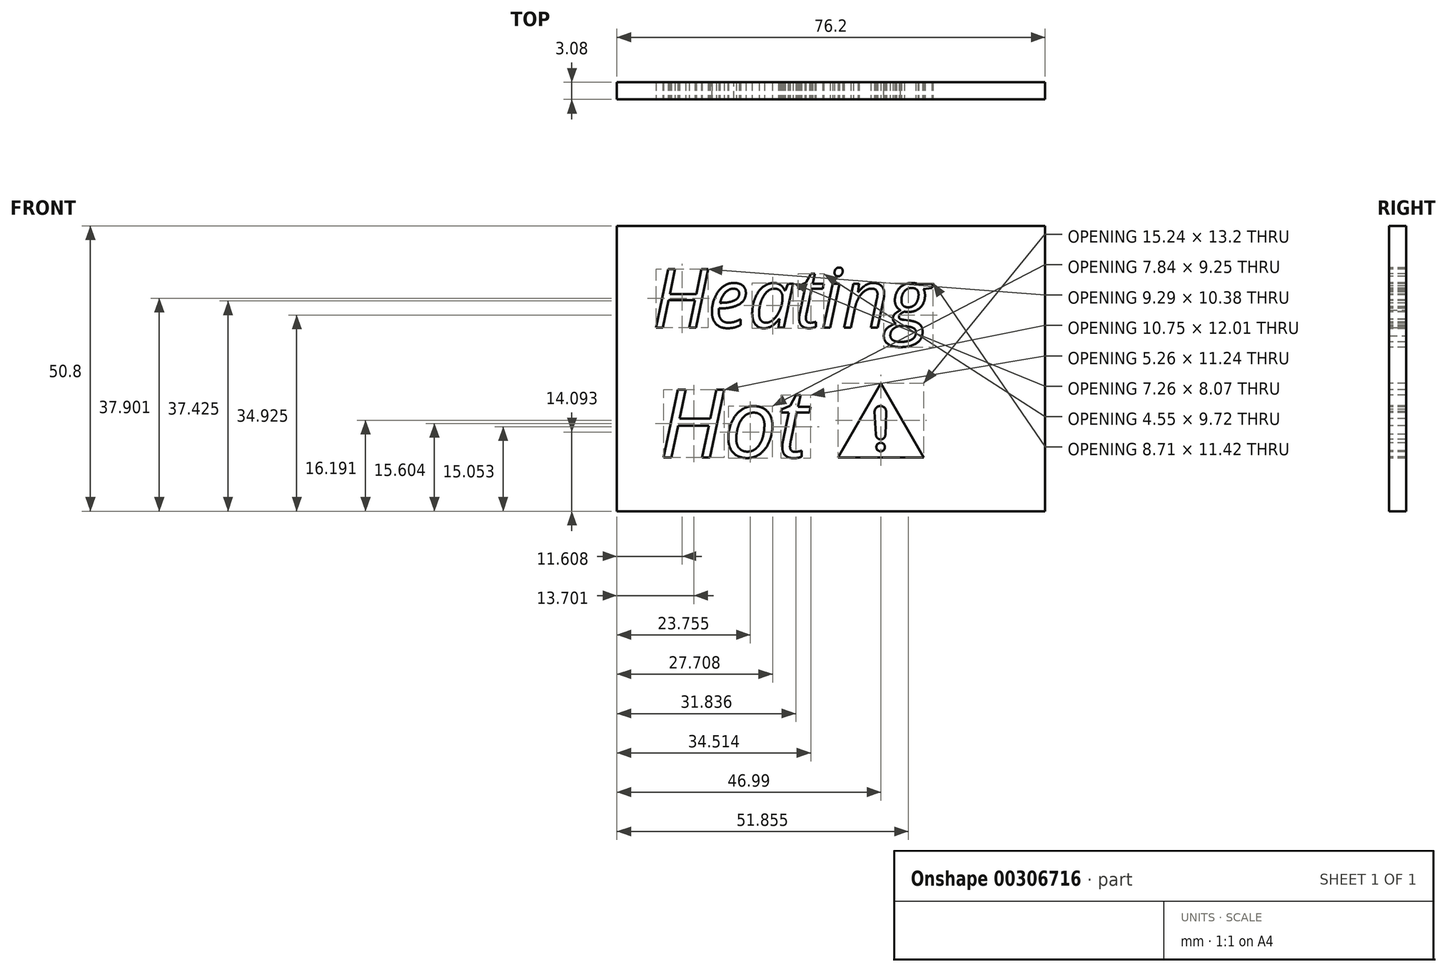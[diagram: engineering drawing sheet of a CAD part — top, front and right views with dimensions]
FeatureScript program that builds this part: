
annotation { "Feature Type Name" : "Feature", "Feature Type Description" : "" }
export const myFeature = defineFeature(function(context is Context, id is Id, definition is map)
    precondition{}
    {
        {
            var Q0;
            Q0=qCreatedBy(makeId("Top.planeOp"),FACE);
            var sketch = newSketch(context, id + "F0", { "sketchPlane" : qUnion([Q0])});
            skLineSegment(sketch, "E0.bottom", {"start": v(38.1, 1.54) * mm, "end": v(-38.1, 1.54) * mm});
            skLineSegment(sketch, "E0.top", {"start": v(38.1, -1.54) * mm, "end": v(-38.1, -1.54) * mm});
            skLineSegment(sketch, "E0.left", {"start": v(38.1, 1.54) * mm, "end": v(38.1, -1.54) * mm});
            skLineSegment(sketch, "E0.right", {"start": v(-38.1, 1.54) * mm, "end": v(-38.1, -1.54) * mm});
            skPoint(sketch, "E0.middle", {"position": v(0, 0) * mm});
            skSolve(sketch);
        }
        {
            var Q0;
            Q0=makeQuery(id+"F0.imprint","IMPRINT",FACE,{"disambiguationData":[TD([[makeQuery(id+"F0.imprint","IMPRINT",EDGE,{"derivedFrom":sQuery(id+"F0.wireOp",EDGE,"E0.bottom")}),1.0]])]});
            extrude(context, id + "F1", {"entities" : qUnion([Q0]), "depth" : 50.8 * mm});
        }
        {
            var Q0;
            Q0=makeQuery(id+"F1.opExtrude","SWEPT_FACE",FACE,{"disambiguationData":[OSD([sQuery(id+"F0.wireOp",EDGE,"E0.top")])]});
            var sketch = newSketch(context, id + "F2", { "sketchPlane" : qUnion([Q0])});
            skText(sketch, "E1", { "text": "Heating", "fontName": "OpenSans-Italic.ttf"});
            skText(sketch, "E2", { "text": "Hot ", "fontName": "OpenSans-Italic.ttf"});
            skLineSegment(sketch, "E3", {"start": v(1.27, 9.6) * mm, "end": v(8.9, 22.79) * mm});
            skLineSegment(sketch, "E4", {"start": v(1.27, 9.6) * mm, "end": v(16.51, 9.6) * mm});
            skLineSegment(sketch, "E5", {"start": v(16.51, 9.6) * mm, "end": v(8.89, 22.79) * mm});
            skCircle(sketch, "E6", {"center": v(8.83, 11.42) * mm, "radius": 0.76 * mm});
            skLineSegment(sketch, "E7", {"start": v(7.76, 17.77) * mm, "end": v(8, 13.71) * mm});
            skLineSegment(sketch, "E8", {"start": v(9.82, 17.66) * mm, "end": v(9.67, 13.6) * mm});
            skArc(sketch, "E9", {"start": v(8, 13.71) * mm, "mid": v(8.78, 12.79) * mm, "end": v(9.67, 13.6) * mm});
            skArc(sketch, "E10", {"start": v(9.82, 17.66) * mm, "mid": v(8.84, 18.73) * mm, "end": v(7.76, 17.77) * mm});
            const initialGuessF2  = {"E1": [-0.03175, 0.03271, 1, 0, 0.01047], "E2": [-0.03048, 0.0096, 1, 0, 0.01211]};
            skSetInitialGuess(sketch, initialGuessF2);
            skSolve(sketch);
        }
        {
            var Q0;
            Q0=makeQuery(id+"F2.imprint","IMPRINT",FACE,{"disambiguationData":[TD([[makeQuery(id+"F2.imprint","IMPRINT",EDGE,{"derivedFrom":sQuery(id+"F2.wireOp",EDGE,"E1.sketch_text.stroke-0")}),-1.0]])]});
            var Q1;
            Q1=makeQuery(id+"F2.imprint","IMPRINT",FACE,{"disambiguationData":[TD([[makeQuery(id+"F2.imprint","IMPRINT",EDGE,{"derivedFrom":sQuery(id+"F2.wireOp",EDGE,"E1.sketch_text.stroke-12")}),-1.0]])]});
            var Q2;
            Q2=makeQuery(id+"F2.imprint","IMPRINT",FACE,{"disambiguationData":[TD([[makeQuery(id+"F2.imprint","IMPRINT",EDGE,{"derivedFrom":sQuery(id+"F2.wireOp",EDGE,"E1.sketch_text.stroke-37")}),-1.0]])]});
            var Q3;
            Q3=makeQuery(id+"F2.imprint","IMPRINT",FACE,{"disambiguationData":[TD([[makeQuery(id+"F2.imprint","IMPRINT",EDGE,{"derivedFrom":sQuery(id+"F2.wireOp",EDGE,"E1.sketch_text.stroke-62")}),-1.0]])]});
            var Q4;
            Q4=makeQuery(id+"F2.imprint","IMPRINT",FACE,{"disambiguationData":[TD([[makeQuery(id+"F2.imprint","IMPRINT",EDGE,{"derivedFrom":sQuery(id+"F2.wireOp",EDGE,"E1.sketch_text.stroke-83")}),-1.0]])]});
            var Q5;
            Q5=makeQuery(id+"F2.imprint","IMPRINT",FACE,{"disambiguationData":[TD([[makeQuery(id+"F2.imprint","IMPRINT",EDGE,{"derivedFrom":sQuery(id+"F2.wireOp",EDGE,"E1.sketch_text.stroke-87")}),-1.0]])]});
            var Q6;
            Q6=makeQuery(id+"F2.imprint","IMPRINT",FACE,{"disambiguationData":[TD([[makeQuery(id+"F2.imprint","IMPRINT",EDGE,{"derivedFrom":sQuery(id+"F2.wireOp",EDGE,"E1.sketch_text.stroke-94")}),-1.0]])]});
            var Q7;
            Q7=makeQuery(id+"F2.imprint","IMPRINT",FACE,{"disambiguationData":[TD([[makeQuery(id+"F2.imprint","IMPRINT",EDGE,{"derivedFrom":sQuery(id+"F2.wireOp",EDGE,"E1.sketch_text.stroke-114")}),-1.0]])]});
            var Q8;
            Q8=makeQuery(id+"F2.imprint","IMPRINT",FACE,{"disambiguationData":[TD([[makeQuery(id+"F2.imprint","IMPRINT",EDGE,{"derivedFrom":sQuery(id+"F2.wireOp",EDGE,"E3")}),-1.0]])]});
            var Q9;
            Q9=makeQuery(id+"F2.imprint","IMPRINT",FACE,{"disambiguationData":[TD([[makeQuery(id+"F2.imprint","IMPRINT",EDGE,{"derivedFrom":sQuery(id+"F2.wireOp",EDGE,"E2.sketch_text.stroke-32")}),-1.0]])]});
            var Q10;
            Q10=makeQuery(id+"F2.imprint","IMPRINT",FACE,{"disambiguationData":[TD([[makeQuery(id+"F2.imprint","IMPRINT",EDGE,{"derivedFrom":sQuery(id+"F2.wireOp",EDGE,"E2.sketch_text.stroke-12")}),-1.0]])]});
            var Q11;
            Q11=makeQuery(id+"F2.imprint","IMPRINT",FACE,{"disambiguationData":[TD([[makeQuery(id+"F2.imprint","IMPRINT",EDGE,{"derivedFrom":sQuery(id+"F2.wireOp",EDGE,"E2.sketch_text.stroke-0")}),-1.0]])]});
            extrude(context, id + "F3", {"entities" : qUnion([Q0, Q1, Q2, Q3, Q4, Q5, Q6, Q7, Q8, Q9, Q10, Q11]), "operationType" : NewBodyOperationType.REMOVE, "oppositeDirection" : true, "depth" : 25.4 * mm});
        }
    });
